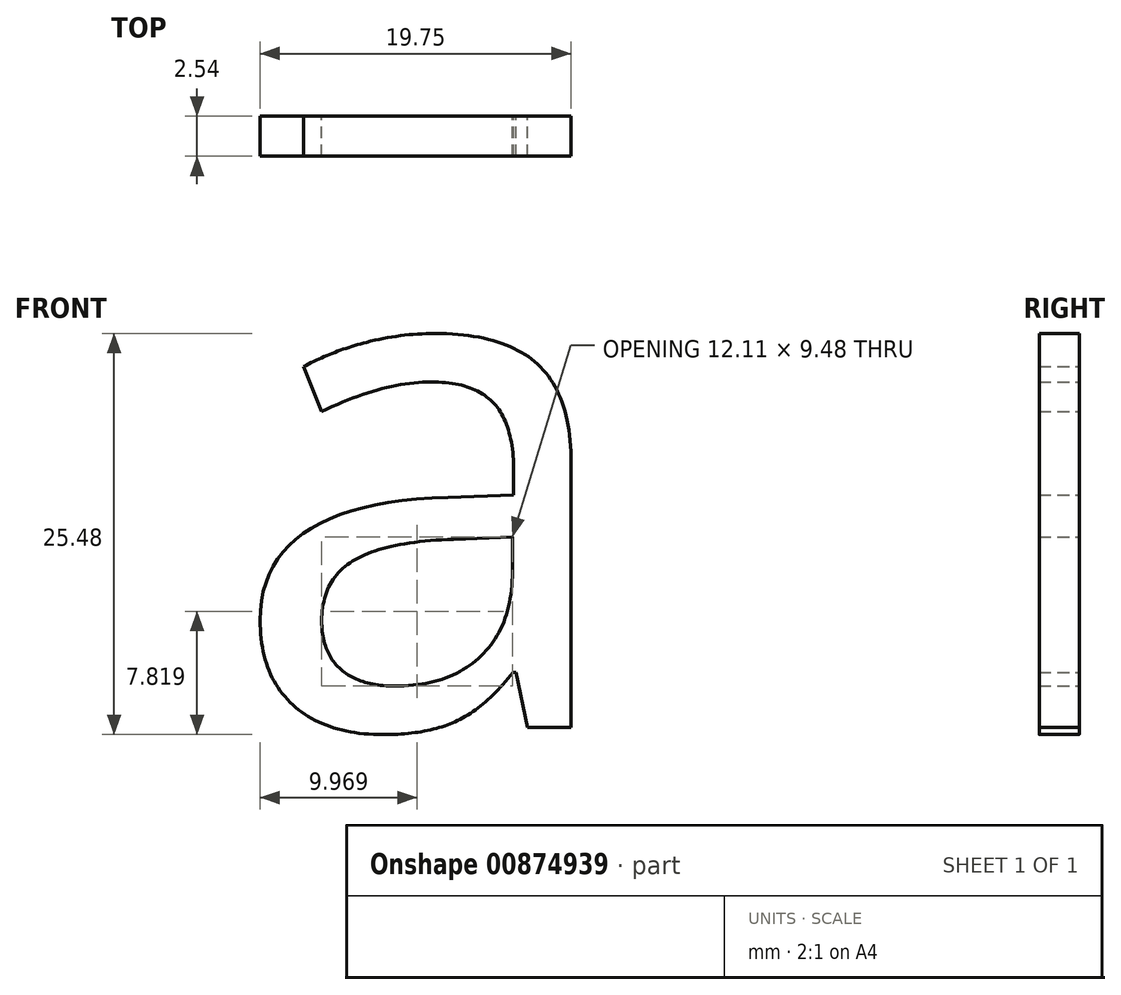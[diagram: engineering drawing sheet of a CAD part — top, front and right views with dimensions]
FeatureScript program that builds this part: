
annotation { "Feature Type Name" : "Feature", "Feature Type Description" : "" }
export const myFeature = defineFeature(function(context is Context, id is Id, definition is map)
    precondition{}
    {
        {
            var Q0;
            Q0=qCreatedBy(makeId("Front.planeOp"),FACE);
            var sketch = newSketch(context, id + "F0", { "sketchPlane" : qUnion([Q0])});
            skText(sketch, "E0", { "text": "a", "fontName": "OpenSans-Regular.ttf"});
            const initialGuessF0  = {"E0": [-0.02485, 0, 1, 0, 0.03313]};
            skSetInitialGuess(sketch, initialGuessF0);
            skSolve(sketch);
        }
        {
            var Q0;
            Q0 = qSketchRegion(id + "F0", true);
            extrude(context, id + "F1", {"entities" : qUnion([Q0]), "depth" : 2.54 * mm, "offsetDistance" : 25.4 * mm});
        }
    });
